# Revit family: GRIFO BAÑO-DUCHA KARIM DUE con accesorios de ducha
name_source: partatom
category: Aparatos sanitarios
revit_build: Autodesk Revit 2015 (Build: 20140223_1515(x64)
units: mm (PartAtom-declared; Revit-internal decimal feet)

## types (1)
- 88941000
    Accionamiento = Por maneta
    CAUDAL = 20,2 l/min a 3 bar
    Comentarios de tipo = ◦Grifo monomando baño ducha ecológico
◦Acabado Cromo
◦Disponible: sin o con accesorios de ducha
◦Cartucho con discos cerámicos de diámetro 35 mm
    Conexión AC = Sí
    Conexión AF = Sí
    Código de montaje = C1030220
    Descripción = Grifo monomando baño ducha. Esta serie de diseño tubular con cuerpo consistente y ergonomía funcional, proporciona una mezcla de estética sencilla y funcionalidad apta para todo tipo de usuarios y ambientes de baño. KARIM aporta el sistema de ahorro de agua Flowing Ecosystem con sistema de doble posición de maneta que permite ahorrar hasta un 50 % de agua. Estético, moderno, funcional y ecológico, así es KARIM DUE.
    ENTRADA = Hembra 3/4" a 1/2" con excéntrica
    Elevación por defecto = 1219 mm
    Fabricante = PRESTO IBÉRICA
    Imagen de tipo = <Ninguno>
    Material = LATON CROMADO
    Modelo = KARIM DUE
    Presión Máxima = 5 bar
    REFERENCIA = 88941000
    TIPO DE AGUA = Fria/Caliente
    Teléfono = (+34) 915 782 575
    URL = http://www.griferiasgalindo.com
